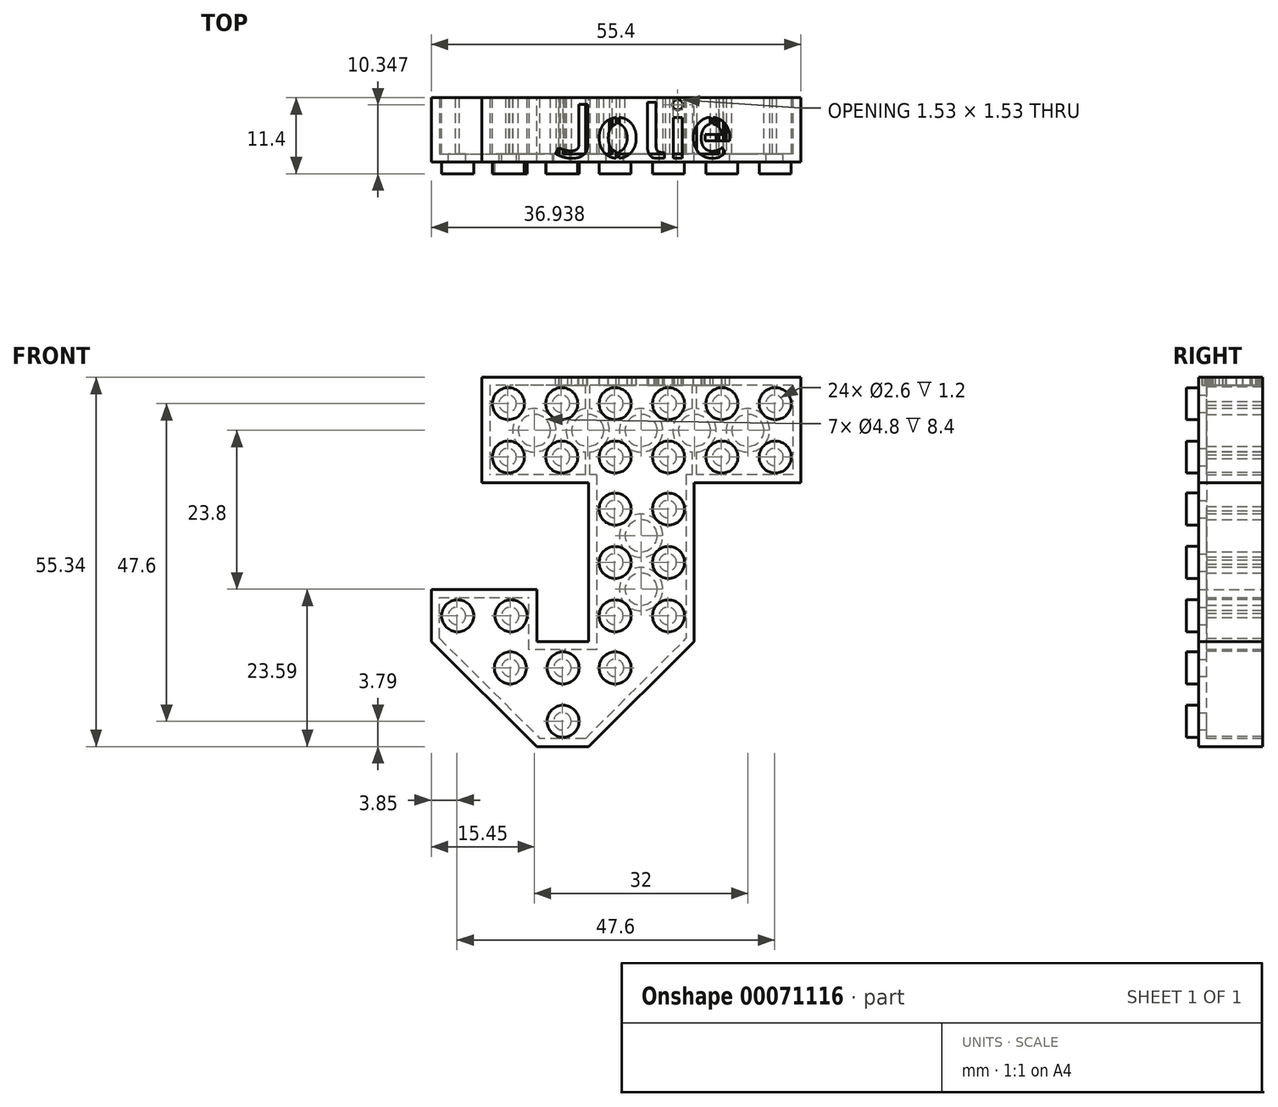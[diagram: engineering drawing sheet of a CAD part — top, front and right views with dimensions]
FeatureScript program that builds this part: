
annotation { "Feature Type Name" : "Feature", "Feature Type Description" : "" }
export const myFeature = defineFeature(function(context is Context, id is Id, definition is map)
    precondition{}
    {
        {
            var Q0;
            Q0=qCreatedBy(makeId("Front.planeOp"),FACE);
            var sketch = newSketch(context, id + "F0", { "sketchPlane" : qUnion([Q0])});
            skLineSegment(sketch, "E0.rect.bottom", {"start": v(23.9, 7.9) * mm, "end": v(-23.9, 7.9) * mm});
            skLineSegment(sketch, "E0.rect.top", {"start": v(23.9, -7.9) * mm, "end": v(7.9, -7.9) * mm});
            skLineSegment(sketch, "E0.rect.left", {"start": v(23.9, 7.9) * mm, "end": v(23.9, -7.9) * mm});
            skLineSegment(sketch, "E0.rect.right", {"start": v(-23.9, 7.9) * mm, "end": v(-23.9, -7.9) * mm});
            skPoint(sketch, "E0.rect.middle", {"position": v(0, 0) * mm});
            skLineSegment(sketch, "E1.left", {"start": v(-7.9, -7.9) * mm, "end": v(-7.9, -31.7) * mm});
            skLineSegment(sketch, "E1.right", {"start": v(7.9, -7.9) * mm, "end": v(7.9, -31.7) * mm});
            skLineSegment(sketch, "E2", {"start": v(-7.9, -47.44) * mm, "end": v(7.9, -31.7) * mm});
            skLineSegment(sketch, "E3.bottom", {"start": v(-7.9, -31.7) * mm, "end": v(-15.7, -31.7) * mm});
            skLineSegment(sketch, "E3.top", {"start": v(-7.9, -47.44) * mm, "end": v(-15.7, -47.44) * mm});
            skLineSegment(sketch, "E4", {"start": v(-31.5, -31.7) * mm, "end": v(-15.7, -47.44) * mm});
            skLineSegment(sketch, "E5.right", {"start": v(-15.7, -31.7) * mm, "end": v(-15.7, -23.9) * mm});
            skLineSegment(sketch, "E5.left", {"start": v(-31.5, -31.7) * mm, "end": v(-31.5, -23.9) * mm});
            skLineSegment(sketch, "E5.top", {"start": v(-31.5, -23.9) * mm, "end": v(-15.7, -23.9) * mm});
            skLineSegment(sketch, "E6.trimOffspring", {"start": v(-7.9, -7.9) * mm, "end": v(-23.9, -7.9) * mm});
            skLineSegment(sketch, "E7", {"start": v(7.9, -7.9) * mm, "end": v(-7.9, -7.9) * mm, "construction": true});
            skLineSegment(sketch, "E8", {"start": v(7.9, -31.7) * mm, "end": v(-7.9, -31.7) * mm, "construction": true});
            skLineSegment(sketch, "E9", {"start": v(-7.9, -31.7) * mm, "end": v(-7.9, -31.7) * mm});
            skLineSegment(sketch, "E10", {"start": v(-7.9, -47.44) * mm, "end": v(-7.9, -31.7) * mm, "construction": true});
            skLineSegment(sketch, "E11", {"start": v(-15.7, -31.7) * mm, "end": v(-15.7, -47.44) * mm, "construction": true});
            skLineSegment(sketch, "E12", {"start": v(-15.7, -31.7) * mm, "end": v(-31.5, -31.7) * mm, "construction": true});
            skSolve(sketch);
        }
        {
            var Q0;
            Q0 = qSketchRegion(id + "F0", true);
            extrude(context, id + "F1", {"entities" : qUnion([Q0]), "depth" : 9.6 * mm});
        }
        {
            var Q0;
            Q0=makeQuery(id+"F0.imprint","IMPRINT",FACE,{"disambiguationData":[TD([[makeQuery(id+"F0.imprint","IMPRINT",EDGE,{"derivedFrom":sQuery(id+"F0.wireOp",EDGE,"E0.rect.bottom")}),1.0]])]});
            var sketch = newSketch(context, id + "F2", { "sketchPlane" : qUnion([Q0])});
            skLineSegment(sketch, "E13.0", {"start": v(-30.3, -31.2) * mm, "end": v(-16.9, -44.55) * mm});
            skLineSegment(sketch, "E13.1", {"start": v(-8.4, -46.24) * mm, "end": v(5, -32.9) * mm});
            skLineSegment(sketch, "E13.2", {"start": v(-8.4, -46.24) * mm, "end": v(-15.2, -46.24) * mm});
            skLineSegment(sketch, "E13.3", {"start": v(-6.7, -44.55) * mm, "end": v(6.7, -31.2) * mm});
            skLineSegment(sketch, "E13.4", {"start": v(-6.7, -32.9) * mm, "end": v(-16.9, -32.9) * mm});
            skLineSegment(sketch, "E13.5", {"start": v(-30.3, -31.2) * mm, "end": v(-30.3, -25.1) * mm});
            skLineSegment(sketch, "E13.6", {"start": v(-6.7, -6.7) * mm, "end": v(-6.7, -32.9) * mm});
            skLineSegment(sketch, "E13.7", {"start": v(-16.9, -32.9) * mm, "end": v(-16.9, -25.1) * mm});
            skLineSegment(sketch, "E13.8", {"start": v(-22.7, 6.7) * mm, "end": v(-22.7, -6.7) * mm});
            skLineSegment(sketch, "E13.9", {"start": v(6.7, -6.7) * mm, "end": v(6.7, -31.2) * mm});
            skLineSegment(sketch, "E13.10", {"start": v(-30.3, -25.1) * mm, "end": v(-16.9, -25.1) * mm});
            skLineSegment(sketch, "E13.11", {"start": v(-6.7, -6.7) * mm, "end": v(-22.7, -6.7) * mm});
            skLineSegment(sketch, "E13.12", {"start": v(22.7, 6.7) * mm, "end": v(-22.7, 6.7) * mm});
            skLineSegment(sketch, "E13.13", {"start": v(-28.6, -32.9) * mm, "end": v(-15.2, -46.24) * mm});
            skLineSegment(sketch, "E13.14", {"start": v(22.7, -6.7) * mm, "end": v(6.7, -6.7) * mm});
            skLineSegment(sketch, "E13.15", {"start": v(22.7, 6.7) * mm, "end": v(22.7, -6.7) * mm});
            skLineSegment(sketch, "E14.2", {"start": v(-15.2, -46.24) * mm, "end": v(-8.4, -46.24) * mm});
            skLineSegment(sketch, "E14.5", {"start": v(-30.3, -25.1) * mm, "end": v(-30.3, -31.2) * mm});
            skLineSegment(sketch, "E14.6", {"start": v(-22.7, -6.7) * mm, "end": v(-6.7, -6.7) * mm});
            skLineSegment(sketch, "E14.10", {"start": v(-16.9, -25.1) * mm, "end": v(-30.3, -25.1) * mm});
            skLineSegment(sketch, "E14.12", {"start": v(22.7, -6.7) * mm, "end": v(22.7, 6.7) * mm});
            skLineSegment(sketch, "E14.14", {"start": v(6.7, -31.2) * mm, "end": v(6.7, -6.7) * mm});
            skLineSegment(sketch, "E14.15", {"start": v(6.7, -6.7) * mm, "end": v(22.7, -6.7) * mm});
            skSolve(sketch);
        }
        {
            var Q0;
            Q0 = qSketchRegion(id + "F2", true);
            extrude(context, id + "F3", {"entities" : qUnion([Q0]), "operationType" : NewBodyOperationType.REMOVE, "depth" : 8.4 * mm});
        }
        {
            var Q0;
            Q0=makeQuery(id+"F1.opExtrude","CAP_FACE",FACE,{"disambiguationData":[OSD([sQuery(id+"F0.wireOp",EDGE,"E0.rect.bottom"),sQuery(id+"F0.wireOp",EDGE,"E0.rect.top"),sQuery(id+"F0.wireOp",EDGE,"E0.rect.left"),sQuery(id+"F0.wireOp",EDGE,"E0.rect.right"),sQuery(id+"F0.wireOp",EDGE,"E1.top"),sQuery(id+"F0.wireOp",EDGE,"E1.left"),sQuery(id+"F0.wireOp",EDGE,"E1.right")])],"isStart":false});
            var sketch = newSketch(context, id + "F4", { "sketchPlane" : qUnion([Q0])});
            skCircle(sketch, "E15", {"center": v(-19.95, 3.95) * mm, "radius": 2.4 * mm});
            skCircle(sketch, "E16.0.1.0", {"center": v(-19.95, -4.05) * mm, "radius": 2.4 * mm});
            skCircle(sketch, "E16.1.0.0", {"center": v(-11.95, 3.95) * mm, "radius": 2.4 * mm});
            skCircle(sketch, "E16.1.1.0", {"center": v(-11.95, -4.05) * mm, "radius": 2.4 * mm});
            skCircle(sketch, "E16.2.0.0", {"center": v(-3.95, 3.95) * mm, "radius": 2.4 * mm});
            skCircle(sketch, "E16.2.1.0", {"center": v(-3.95, -4.05) * mm, "radius": 2.4 * mm});
            skCircle(sketch, "E16.3.0.0", {"center": v(4.05, 3.95) * mm, "radius": 2.4 * mm});
            skCircle(sketch, "E16.3.1.0", {"center": v(4.05, -4.05) * mm, "radius": 2.4 * mm});
            skCircle(sketch, "E16.4.0.0", {"center": v(12.05, 3.95) * mm, "radius": 2.4 * mm});
            skCircle(sketch, "E16.4.1.0", {"center": v(12.05, -4.05) * mm, "radius": 2.4 * mm});
            skCircle(sketch, "E16.5.0.0", {"center": v(20.05, 3.95) * mm, "radius": 2.4 * mm});
            skCircle(sketch, "E16.5.1.0", {"center": v(20.05, -4.05) * mm, "radius": 2.4 * mm});
            skLineSegment(sketch, "E16.direction1", {"start": v(-19.95, 3.95) * mm, "end": v(-11.95, 3.95) * mm, "construction": true});
            skLineSegment(sketch, "E16.direction2", {"start": v(-19.95, 3.95) * mm, "end": v(-19.95, -4.05) * mm, "construction": true});
            skSolve(sketch);
        }
        {
            var Q0;
            Q0=makeQuery(id+"F4.imprint","IMPRINT",FACE,{"disambiguationData":[TD([[makeQuery(id+"F4.imprint","IMPRINT",EDGE,{"derivedFrom":sQuery(id+"F4.wireOp",EDGE,"E15")}),1.0]])]});
            var Q1;
            Q1=makeQuery(id+"F4.imprint","IMPRINT",FACE,{"disambiguationData":[TD([[makeQuery(id+"F4.imprint","IMPRINT",EDGE,{"derivedFrom":sQuery(id+"F4.wireOp",EDGE,"E16.0.1.0")}),1.0]])]});
            var Q2;
            Q2=makeQuery(id+"F4.imprint","IMPRINT",FACE,{"disambiguationData":[TD([[makeQuery(id+"F4.imprint","IMPRINT",EDGE,{"derivedFrom":sQuery(id+"F4.wireOp",EDGE,"E16.1.0.0")}),1.0]])]});
            var Q3;
            Q3=makeQuery(id+"F4.imprint","IMPRINT",FACE,{"disambiguationData":[TD([[makeQuery(id+"F4.imprint","IMPRINT",EDGE,{"derivedFrom":sQuery(id+"F4.wireOp",EDGE,"E16.1.1.0")}),1.0]])]});
            var Q4;
            Q4=makeQuery(id+"F4.imprint","IMPRINT",FACE,{"disambiguationData":[TD([[makeQuery(id+"F4.imprint","IMPRINT",EDGE,{"derivedFrom":sQuery(id+"F4.wireOp",EDGE,"E16.2.0.0")}),1.0]])]});
            var Q5;
            Q5=makeQuery(id+"F4.imprint","IMPRINT",FACE,{"disambiguationData":[TD([[makeQuery(id+"F4.imprint","IMPRINT",EDGE,{"derivedFrom":sQuery(id+"F4.wireOp",EDGE,"E16.2.1.0")}),1.0]])]});
            var Q6;
            Q6=makeQuery(id+"F4.imprint","IMPRINT",FACE,{"disambiguationData":[TD([[makeQuery(id+"F4.imprint","IMPRINT",EDGE,{"derivedFrom":sQuery(id+"F4.wireOp",EDGE,"E16.3.0.0")}),1.0]])]});
            var Q7;
            Q7=makeQuery(id+"F4.imprint","IMPRINT",FACE,{"disambiguationData":[TD([[makeQuery(id+"F4.imprint","IMPRINT",EDGE,{"derivedFrom":sQuery(id+"F4.wireOp",EDGE,"E16.3.1.0")}),1.0]])]});
            var Q8;
            Q8=makeQuery(id+"F4.imprint","IMPRINT",FACE,{"disambiguationData":[TD([[makeQuery(id+"F4.imprint","IMPRINT",EDGE,{"derivedFrom":sQuery(id+"F4.wireOp",EDGE,"E16.4.0.0")}),1.0]])]});
            var Q9;
            Q9=makeQuery(id+"F4.imprint","IMPRINT",FACE,{"disambiguationData":[TD([[makeQuery(id+"F4.imprint","IMPRINT",EDGE,{"derivedFrom":sQuery(id+"F4.wireOp",EDGE,"E16.4.1.0")}),1.0]])]});
            var Q10;
            Q10=makeQuery(id+"F4.imprint","IMPRINT",FACE,{"disambiguationData":[TD([[makeQuery(id+"F4.imprint","IMPRINT",EDGE,{"derivedFrom":sQuery(id+"F4.wireOp",EDGE,"E16.5.0.0")}),1.0]])]});
            var Q11;
            Q11=makeQuery(id+"F4.imprint","IMPRINT",FACE,{"disambiguationData":[TD([[makeQuery(id+"F4.imprint","IMPRINT",EDGE,{"derivedFrom":sQuery(id+"F4.wireOp",EDGE,"E16.5.1.0")}),1.0]])]});
            extrude(context, id + "F5", {"entities" : qUnion([Q0, Q1, Q2, Q3, Q4, Q5, Q6, Q7, Q8, Q9, Q10, Q11]), "operationType" : NewBodyOperationType.ADD, "depth" : 1.8 * mm});
        }
        {
            var Q0;
            Q0=makeQuery(id+"F4.imprint","IMPRINT",FACE,{"disambiguationData":[TD([[makeQuery(id+"F4.imprint","IMPRINT",EDGE,{"derivedFrom":sQuery(id+"F4.wireOp",EDGE,"E15")}),-1.0]])]});
            var sketch = newSketch(context, id + "F6", { "sketchPlane" : qUnion([Q0])});
            skCircle(sketch, "E17", {"center": v(-3.95, -11.85) * mm, "radius": 2.4 * mm});
            skCircle(sketch, "E18.0.1.0", {"center": v(-3.95, -19.85) * mm, "radius": 2.4 * mm});
            skCircle(sketch, "E18.0.2.0", {"center": v(-3.95, -27.85) * mm, "radius": 2.4 * mm});
            skCircle(sketch, "E18.1.0.0", {"center": v(4.05, -11.85) * mm, "radius": 2.4 * mm});
            skCircle(sketch, "E18.1.1.0", {"center": v(4.05, -19.85) * mm, "radius": 2.4 * mm});
            skCircle(sketch, "E18.1.2.0", {"center": v(4.05, -27.85) * mm, "radius": 2.4 * mm});
            skLineSegment(sketch, "E18.direction1", {"start": v(-3.95, -11.85) * mm, "end": v(4.05, -11.85) * mm, "construction": true});
            skLineSegment(sketch, "E18.direction2", {"start": v(-3.95, -11.85) * mm, "end": v(-3.95, -19.85) * mm, "construction": true});
            skSolve(sketch);
        }
        {
            var Q0;
            Q0 = qSketchRegion(id + "F6", true);
            extrude(context, id + "F7", {"entities" : qUnion([Q0]), "operationType" : NewBodyOperationType.ADD, "depth" : 1.8 * mm});
        }
        {
            var Q0;
            Q0=makeQuery(id+"F4.imprint","IMPRINT",FACE,{"disambiguationData":[TD([[makeQuery(id+"F4.imprint","IMPRINT",EDGE,{"derivedFrom":sQuery(id+"F4.wireOp",EDGE,"E15")}),-1.0]])]});
            var sketch = newSketch(context, id + "F8", { "sketchPlane" : qUnion([Q0])});
            skCircle(sketch, "E19", {"center": v(-11.75, -35.65) * mm, "radius": 2.4 * mm});
            skCircle(sketch, "E20.0.1.0", {"center": v(-11.75, -43.65) * mm, "radius": 2.4 * mm});
            skCircle(sketch, "E21", {"center": v(-27.55, -27.85) * mm, "radius": 2.4 * mm});
            skCircle(sketch, "E22.1.0.0", {"center": v(-19.55, -27.85) * mm, "radius": 2.4 * mm});
            skLineSegment(sketch, "E23", {"start": v(-11.75, -43.65) * mm, "end": v(-11.75, -35.65) * mm, "construction": true});
            skSolve(sketch);
        }
        {
            var Q0;
            Q0 = qSketchRegion(id + "F8", true);
            extrude(context, id + "F9", {"entities" : qUnion([Q0]), "operationType" : NewBodyOperationType.ADD, "depth" : 1.8 * mm});
        }
        {
            var Q0;
            Q0=makeQuery(id+"F8.imprint","IMPRINT",FACE,{"disambiguationData":[TD([[makeQuery(id+"F8.imprint","IMPRINT",EDGE,{"derivedFrom":sQuery(id+"F8.wireOp",EDGE,"E19")}),-1.0]])]});
            var sketch = newSketch(context, id + "F10", { "sketchPlane" : qUnion([Q0])});
            skCircle(sketch, "E24", {"center": v(-3.95, -35.65) * mm, "radius": 2.4 * mm});
            skCircle(sketch, "E25", {"center": v(-19.65, -35.65) * mm, "radius": 2.4 * mm});
            skSolve(sketch);
        }
        {
            var Q0;
            Q0 = qSketchRegion(id + "F10", true);
            extrude(context, id + "F11", {"entities" : qUnion([Q0]), "operationType" : NewBodyOperationType.ADD, "depth" : 1.8 * mm});
        }
        {
            var Q0;
            Q0=makeQuery(id+"F0.imprint","IMPRINT",FACE,{"disambiguationData":[TD([[makeQuery(id+"F0.imprint","IMPRINT",EDGE,{"derivedFrom":sQuery(id+"F0.wireOp",EDGE,"E0.rect.bottom")}),1.0]])]});
            cPlane(context, id + "F12", {"entities" : qUnion([Q0]), "cplaneType" : CPlaneType.OFFSET, "offset" : 8.4 * mm, "width" : 150 * mm, "height" : 150 * mm});
        }
        {
            var Q0;
            Q0=qCreatedBy(id+"F12.planeOp",FACE);
            var sketch = newSketch(context, id + "F13", { "sketchPlane" : qUnion([Q0])});
            skCircle(sketch, "E26", {"center": v(19.95, 3.95) * mm, "radius": 1.3 * mm});
            skCircle(sketch, "E27.0.1.0", {"center": v(19.95, -4.05) * mm, "radius": 1.3 * mm});
            skCircle(sketch, "E27.1.0.0", {"center": v(11.95, 3.95) * mm, "radius": 1.3 * mm});
            skCircle(sketch, "E27.1.1.0", {"center": v(11.95, -4.05) * mm, "radius": 1.3 * mm});
            skCircle(sketch, "E27.2.0.0", {"center": v(3.95, 3.95) * mm, "radius": 1.3 * mm});
            skCircle(sketch, "E27.2.1.0", {"center": v(3.95, -4.05) * mm, "radius": 1.3 * mm});
            skCircle(sketch, "E27.3.0.0", {"center": v(-4.05, 3.95) * mm, "radius": 1.3 * mm});
            skCircle(sketch, "E27.3.1.0", {"center": v(-4.05, -4.05) * mm, "radius": 1.3 * mm});
            skCircle(sketch, "E27.4.0.0", {"center": v(-12.05, 3.95) * mm, "radius": 1.3 * mm});
            skCircle(sketch, "E27.4.1.0", {"center": v(-12.05, -4.05) * mm, "radius": 1.3 * mm});
            skCircle(sketch, "E27.5.0.0", {"center": v(-20.05, 3.95) * mm, "radius": 1.3 * mm});
            skCircle(sketch, "E27.5.1.0", {"center": v(-20.05, -4.05) * mm, "radius": 1.3 * mm});
            skLineSegment(sketch, "E27.direction1", {"start": v(19.95, 3.95) * mm, "end": v(11.95, 3.95) * mm, "construction": true});
            skLineSegment(sketch, "E27.direction2", {"start": v(19.95, 3.95) * mm, "end": v(19.95, -4.05) * mm, "construction": true});
            skCircle(sketch, "E28", {"center": v(3.95, -11.85) * mm, "radius": 1.3 * mm});
            skCircle(sketch, "E29.0.1.0", {"center": v(3.95, -19.85) * mm, "radius": 1.3 * mm});
            skCircle(sketch, "E29.0.2.0", {"center": v(3.95, -27.85) * mm, "radius": 1.3 * mm});
            skCircle(sketch, "E29.1.0.0", {"center": v(-4.05, -11.85) * mm, "radius": 1.3 * mm});
            skCircle(sketch, "E29.1.1.0", {"center": v(-4.05, -19.85) * mm, "radius": 1.3 * mm});
            skCircle(sketch, "E29.1.2.0", {"center": v(-4.05, -27.85) * mm, "radius": 1.3 * mm});
            skLineSegment(sketch, "E29.direction1", {"start": v(3.95, -11.85) * mm, "end": v(-4.05, -11.85) * mm, "construction": true});
            skLineSegment(sketch, "E29.direction2", {"start": v(3.95, -11.85) * mm, "end": v(3.95, -19.85) * mm, "construction": true});
            skCircle(sketch, "E30", {"center": v(-3.95, -35.65) * mm, "radius": 1.3 * mm});
            skCircle(sketch, "E31", {"center": v(-11.85, -35.65) * mm, "radius": 1.3 * mm});
            skCircle(sketch, "E32", {"center": v(-19.65, -35.65) * mm, "radius": 1.3 * mm});
            skCircle(sketch, "E33", {"center": v(-19.65, -27.85) * mm, "radius": 1.3 * mm});
            skCircle(sketch, "E34", {"center": v(-11.85, -43.65) * mm, "radius": 1.3 * mm});
            skCircle(sketch, "E35", {"center": v(-27.65, -27.85) * mm, "radius": 1.3 * mm});
            skSolve(sketch);
        }
        {
            var Q0;
            Q0 = qSketchRegion(id + "F13", true);
            extrude(context, id + "F14", {"entities" : qUnion([Q0]), "operationType" : NewBodyOperationType.REMOVE, "depth" : 1.2 * mm});
        }
        {
            var Q0;
            Q0=qCreatedBy(id+"F12.planeOp",FACE);
            var sketch = newSketch(context, id + "F15", { "sketchPlane" : qUnion([Q0])});
            skLineSegment(sketch, "E36", {"start": v(22.74, 6.74) * mm, "end": v(9.34, -6.66) * mm, "construction": true});
            skLineSegment(sketch, "E37", {"start": v(22.7, -6.8) * mm, "end": v(9.62, 6.28) * mm, "construction": true});
            skCircle(sketch, "E38", {"center": v(15.95, -0.05) * mm, "radius": 3.25 * mm});
            skCircle(sketch, "E39.1.0.0", {"center": v(7.95, -0.05) * mm, "radius": 3.25 * mm});
            skCircle(sketch, "E39.2.0.0", {"center": v(-0.05, -0.05) * mm, "radius": 3.25 * mm});
            skCircle(sketch, "E39.3.0.0", {"center": v(-8.05, -0.05) * mm, "radius": 3.25 * mm});
            skCircle(sketch, "E39.4.0.0", {"center": v(-16.05, -0.05) * mm, "radius": 3.25 * mm});
            skLineSegment(sketch, "E39.direction1", {"start": v(15.95, -0.05) * mm, "end": v(7.95, -0.05) * mm, "construction": true});
            skLineSegment(sketch, "E40", {"start": v(6.74, -9.06) * mm, "end": v(-5.78, -21.58) * mm, "construction": true});
            skLineSegment(sketch, "E41", {"start": v(6.08, -21.98) * mm, "end": v(-6.32, -9.58) * mm, "construction": true});
            skCircle(sketch, "E42", {"center": v(-0.05, -15.85) * mm, "radius": 3.25 * mm});
            skCircle(sketch, "E43.0.1.0", {"center": v(-0.05, -23.85) * mm, "radius": 3.25 * mm});
            skLineSegment(sketch, "E43.direction1", {"start": v(-0.05, -15.85) * mm, "end": v(7.95, -15.85) * mm, "construction": true});
            skLineSegment(sketch, "E43.direction2", {"start": v(-0.05, -15.85) * mm, "end": v(-0.05, -23.85) * mm, "construction": true});
            skSolve(sketch);
        }
        {
            var Q0;
            Q0 = qSketchRegion(id + "F15", true);
            extrude(context, id + "F16", {"entities" : qUnion([Q0]), "operationType" : NewBodyOperationType.ADD, "oppositeDirection" : true, "depth" : 8.4 * mm});
        }
        {
            var Q0;
            Q0=makeQuery(id+"F0.imprint","IMPRINT",FACE,{"disambiguationData":[TD([[makeQuery(id+"F0.imprint","IMPRINT",EDGE,{"derivedFrom":sQuery(id+"F0.wireOp",EDGE,"E0.rect.bottom")}),1.0]])]});
            var sketch = newSketch(context, id + "F17", { "sketchPlane" : qUnion([Q0])});
            skCircle(sketch, "E44", {"center": v(15.95, -0.05) * mm, "radius": 2.4 * mm});
            skCircle(sketch, "E45", {"center": v(-0.05, -15.85) * mm, "radius": 2.4 * mm});
            skCircle(sketch, "E46.1.0.0", {"center": v(7.95, -0.05) * mm, "radius": 2.4 * mm});
            skCircle(sketch, "E46.2.0.0", {"center": v(-0.05, -0.05) * mm, "radius": 2.4 * mm});
            skCircle(sketch, "E46.3.0.0", {"center": v(-8.05, -0.05) * mm, "radius": 2.4 * mm});
            skCircle(sketch, "E46.4.0.0", {"center": v(-16.05, -0.05) * mm, "radius": 2.4 * mm});
            skLineSegment(sketch, "E46.direction1", {"start": v(15.95, -0.05) * mm, "end": v(7.95, -0.05) * mm, "construction": true});
            skCircle(sketch, "E47.0.1.0", {"center": v(-0.05, -23.85) * mm, "radius": 2.4 * mm});
            skLineSegment(sketch, "E47.direction1", {"start": v(-0.05, -15.85) * mm, "end": v(7.95, -15.85) * mm, "construction": true});
            skLineSegment(sketch, "E47.direction2", {"start": v(-0.05, -15.85) * mm, "end": v(-0.05, -23.85) * mm, "construction": true});
            skSolve(sketch);
        }
        {
            var Q0;
            Q0=makeQuery(id+"F17.imprint","IMPRINT",FACE,{"disambiguationData":[TD([[makeQuery(id+"F17.imprint","IMPRINT",EDGE,{"derivedFrom":sQuery(id+"F17.wireOp",EDGE,"E44")}),1.0]])]});
            var Q1;
            Q1=makeQuery(id+"F17.imprint","IMPRINT",FACE,{"disambiguationData":[TD([[makeQuery(id+"F17.imprint","IMPRINT",EDGE,{"derivedFrom":sQuery(id+"F17.wireOp",EDGE,"E46.1.0.0")}),1.0]])]});
            var Q2;
            Q2=makeQuery(id+"F17.imprint","IMPRINT",FACE,{"disambiguationData":[TD([[makeQuery(id+"F17.imprint","IMPRINT",EDGE,{"derivedFrom":sQuery(id+"F17.wireOp",EDGE,"E45")}),1.0]])]});
            var Q3;
            Q3=makeQuery(id+"F17.imprint","IMPRINT",FACE,{"disambiguationData":[TD([[makeQuery(id+"F17.imprint","IMPRINT",EDGE,{"derivedFrom":sQuery(id+"F17.wireOp",EDGE,"E47.0.1.0")}),1.0]])]});
            var Q4;
            Q4=makeQuery(id+"F17.imprint","IMPRINT",FACE,{"disambiguationData":[TD([[makeQuery(id+"F17.imprint","IMPRINT",EDGE,{"derivedFrom":sQuery(id+"F17.wireOp",EDGE,"E46.4.0.0")}),1.0]])]});
            var Q5;
            Q5=makeQuery(id+"F17.imprint","IMPRINT",FACE,{"disambiguationData":[TD([[makeQuery(id+"F17.imprint","IMPRINT",EDGE,{"derivedFrom":sQuery(id+"F17.wireOp",EDGE,"E46.3.0.0")}),1.0]])]});
            var Q6;
            Q6=makeQuery(id+"F17.imprint","IMPRINT",FACE,{"disambiguationData":[TD([[makeQuery(id+"F17.imprint","IMPRINT",EDGE,{"derivedFrom":sQuery(id+"F17.wireOp",EDGE,"E46.2.0.0")}),1.0]])]});
            extrude(context, id + "F18", {"entities" : qUnion([Q0, Q1, Q2, Q3, Q4, Q5, Q6]), "operationType" : NewBodyOperationType.REMOVE, "depth" : 8.4 * mm});
        }
        {
            var Q0;
            Q0=qCreatedBy(id+"F12.planeOp",FACE);
            var sketch = newSketch(context, id + "F19", { "sketchPlane" : qUnion([Q0])});
            skLineSegment(sketch, "E48.bottom", {"start": v(8.25, -6.7) * mm, "end": v(7.65, -6.7) * mm});
            skLineSegment(sketch, "E48.top", {"start": v(8.25, -2.7) * mm, "end": v(7.65, -2.7) * mm});
            skLineSegment(sketch, "E48.left", {"start": v(8.25, -6.7) * mm, "end": v(8.25, -2.7) * mm});
            skLineSegment(sketch, "E48.right", {"start": v(7.65, -6.7) * mm, "end": v(7.65, -2.7) * mm});
            skLineSegment(sketch, "E49.0.1.0", {"start": v(8.25, 2.7) * mm, "end": v(8.25, 6.7) * mm});
            skLineSegment(sketch, "E49.0.1.1", {"start": v(8.25, 6.7) * mm, "end": v(7.65, 6.7) * mm});
            skLineSegment(sketch, "E49.0.1.2", {"start": v(7.65, 2.7) * mm, "end": v(7.65, 6.7) * mm});
            skLineSegment(sketch, "E49.0.1.3", {"start": v(8.25, 2.7) * mm, "end": v(7.65, 2.7) * mm});
            skLineSegment(sketch, "E49.1.0.0", {"start": v(-7.75, -6.7) * mm, "end": v(-7.75, -2.7) * mm});
            skLineSegment(sketch, "E49.1.0.1", {"start": v(-7.75, -2.7) * mm, "end": v(-8.35, -2.7) * mm});
            skLineSegment(sketch, "E49.1.0.2", {"start": v(-8.35, -6.7) * mm, "end": v(-8.35, -2.7) * mm});
            skLineSegment(sketch, "E49.1.0.3", {"start": v(-7.75, -6.7) * mm, "end": v(-8.35, -6.7) * mm});
            skLineSegment(sketch, "E49.1.1.0", {"start": v(-7.75, 2.7) * mm, "end": v(-7.75, 6.7) * mm});
            skLineSegment(sketch, "E49.1.1.1", {"start": v(-7.75, 6.7) * mm, "end": v(-8.35, 6.7) * mm});
            skLineSegment(sketch, "E49.1.1.2", {"start": v(-8.35, 2.7) * mm, "end": v(-8.35, 6.7) * mm});
            skLineSegment(sketch, "E49.1.1.3", {"start": v(-7.75, 2.7) * mm, "end": v(-8.35, 2.7) * mm});
            skLineSegment(sketch, "E49.direction1", {"start": v(8.25, -6.7) * mm, "end": v(-7.75, -6.7) * mm, "construction": true});
            skLineSegment(sketch, "E49.direction2", {"start": v(8.25, -6.7) * mm, "end": v(8.25, 2.7) * mm, "construction": true});
            skSolve(sketch);
        }
        {
            var Q0;
            Q0 = qSketchRegion(id + "F19", true);
            var Q1;
            Q1=makeQuery(id+"F16.boolean.opBoolean","MERGE",FACE,{"derivedFrom":[makeQuery(id+"F1.opExtrude","CAP_FACE",FACE,{"disambiguationData":[OSD([sQuery(id+"F0.wireOp",EDGE,"E0.rect.bottom"),sQuery(id+"F0.wireOp",EDGE,"E0.rect.top"),sQuery(id+"F0.wireOp",EDGE,"E0.rect.left"),sQuery(id+"F0.wireOp",EDGE,"E0.rect.right"),sQuery(id+"F0.wireOp",EDGE,"E1.top"),sQuery(id+"F0.wireOp",EDGE,"E1.left"),sQuery(id+"F0.wireOp",EDGE,"E1.right")])],"isStart":true}),makeQuery(id+"F1.opExtrude","CAP_FACE",FACE,{"disambiguationData":[OSD([sQuery(id+"FJ1ACUDYxAhP0Kk_0.wireOp",EDGE,"Wucu8hu5-kGE4-iVw8-EwE2-y0JzsKfOnsuY"),sQuery(id+"FJ1ACUDYxAhP0Kk_0.wireOp",EDGE,"a33cc1b2-1836-41d1-88ad-fe0056d83a28.bottom"),sQuery(id+"FJ1ACUDYxAhP0Kk_0.wireOp",EDGE,"a33cc1b2-1836-41d1-88ad-fe0056d83a28.top"),sQuery(id+"FJ1ACUDYxAhP0Kk_0.wireOp",EDGE,"7wYbTLAZ-uymM-28nJ-zka1-vrEMmaOiro4r"),sQuery(id+"FJ1ACUDYxAhP0Kk_0.wireOp",EDGE,"40946cf3-8972-4417-9fa9-1b25ef5c2fd7.top"),sQuery(id+"FJ1ACUDYxAhP0Kk_0.wireOp",EDGE,"40946cf3-8972-4417-9fa9-1b25ef5c2fd7.left"),sQuery(id+"FJ1ACUDYxAhP0Kk_0.wireOp",EDGE,"40946cf3-8972-4417-9fa9-1b25ef5c2fd7.right"),sQuery(id+"FJ1ACUDYxAhP0Kk_0.wireOp",EDGE,"NUz24gwK-Pouy-i7gN-xPQZ-Jzt4TPqwj3US")])],"isStart":true})]});
            extrude(context, id + "F20", {"entities" : qUnion([Q0]), "operationType" : NewBodyOperationType.ADD, "endBound" : BoundingType.UP_TO_SURFACE, "oppositeDirection" : true, "endBoundEntityFace" : qUnion([Q1]), "depth" : 25 * mm});
        }
        {
            var Q0;
            Q0=qCreatedBy(id+"F12.planeOp",FACE);
            var sketch = newSketch(context, id + "F21", { "sketchPlane" : qUnion([Q0])});
            skLineSegment(sketch, "E50", {"start": v(19.95, 4) * mm, "end": v(19.95, -10.78) * mm, "construction": true});
            skLineSegment(sketch, "E51.bottom", {"start": v(20.25, -6.4) * mm, "end": v(19.65, -6.4) * mm});
            skLineSegment(sketch, "E51.top", {"start": v(20.25, -6.7) * mm, "end": v(19.65, -6.7) * mm});
            skLineSegment(sketch, "E51.left", {"start": v(19.65, -6.4) * mm, "end": v(19.65, -6.7) * mm});
            skLineSegment(sketch, "E51.right", {"start": v(20.25, -6.4) * mm, "end": v(20.25, -6.7) * mm});
            skLineSegment(sketch, "E52.0.1.0", {"start": v(20.25, 6.72) * mm, "end": v(19.65, 6.72) * mm});
            skLineSegment(sketch, "E52.0.1.1", {"start": v(19.65, 6.72) * mm, "end": v(19.65, 6.42) * mm});
            skLineSegment(sketch, "E52.0.1.2", {"start": v(20.25, 6.42) * mm, "end": v(19.65, 6.42) * mm});
            skLineSegment(sketch, "E52.0.1.3", {"start": v(20.25, 6.72) * mm, "end": v(20.25, 6.42) * mm});
            skLineSegment(sketch, "E52.1.0.0", {"start": v(12.25, -6.4) * mm, "end": v(11.65, -6.4) * mm});
            skLineSegment(sketch, "E52.1.0.1", {"start": v(11.65, -6.4) * mm, "end": v(11.65, -6.7) * mm});
            skLineSegment(sketch, "E52.1.0.2", {"start": v(12.25, -6.7) * mm, "end": v(11.65, -6.7) * mm});
            skLineSegment(sketch, "E52.1.0.3", {"start": v(12.25, -6.4) * mm, "end": v(12.25, -6.7) * mm});
            skLineSegment(sketch, "E52.1.1.0", {"start": v(12.25, 6.72) * mm, "end": v(11.65, 6.72) * mm});
            skLineSegment(sketch, "E52.1.1.1", {"start": v(11.65, 6.72) * mm, "end": v(11.65, 6.42) * mm});
            skLineSegment(sketch, "E52.1.1.2", {"start": v(12.25, 6.42) * mm, "end": v(11.65, 6.42) * mm});
            skLineSegment(sketch, "E52.1.1.3", {"start": v(12.25, 6.72) * mm, "end": v(12.25, 6.42) * mm});
            skLineSegment(sketch, "E52.2.1.0", {"start": v(4.25, 6.72) * mm, "end": v(3.65, 6.72) * mm});
            skLineSegment(sketch, "E52.2.1.1", {"start": v(3.65, 6.72) * mm, "end": v(3.65, 6.42) * mm});
            skLineSegment(sketch, "E52.2.1.2", {"start": v(4.25, 6.42) * mm, "end": v(3.65, 6.42) * mm});
            skLineSegment(sketch, "E52.2.1.3", {"start": v(4.25, 6.72) * mm, "end": v(4.25, 6.42) * mm});
            skLineSegment(sketch, "E52.3.1.0", {"start": v(-3.75, 6.72) * mm, "end": v(-4.35, 6.72) * mm});
            skLineSegment(sketch, "E52.3.1.1", {"start": v(-4.35, 6.72) * mm, "end": v(-4.35, 6.42) * mm});
            skLineSegment(sketch, "E52.3.1.2", {"start": v(-3.75, 6.42) * mm, "end": v(-4.35, 6.42) * mm});
            skLineSegment(sketch, "E52.3.1.3", {"start": v(-3.75, 6.72) * mm, "end": v(-3.75, 6.42) * mm});
            skLineSegment(sketch, "E52.4.0.0", {"start": v(-11.75, -6.4) * mm, "end": v(-12.35, -6.4) * mm});
            skLineSegment(sketch, "E52.4.0.1", {"start": v(-12.35, -6.4) * mm, "end": v(-12.35, -6.7) * mm});
            skLineSegment(sketch, "E52.4.0.2", {"start": v(-11.75, -6.7) * mm, "end": v(-12.35, -6.7) * mm});
            skLineSegment(sketch, "E52.4.0.3", {"start": v(-11.75, -6.4) * mm, "end": v(-11.75, -6.7) * mm});
            skLineSegment(sketch, "E52.4.1.0", {"start": v(-11.75, 6.72) * mm, "end": v(-12.35, 6.72) * mm});
            skLineSegment(sketch, "E52.4.1.1", {"start": v(-12.35, 6.72) * mm, "end": v(-12.35, 6.42) * mm});
            skLineSegment(sketch, "E52.4.1.2", {"start": v(-11.75, 6.42) * mm, "end": v(-12.35, 6.42) * mm});
            skLineSegment(sketch, "E52.4.1.3", {"start": v(-11.75, 6.72) * mm, "end": v(-11.75, 6.42) * mm});
            skLineSegment(sketch, "E52.5.0.0", {"start": v(-19.75, -6.4) * mm, "end": v(-20.35, -6.4) * mm});
            skLineSegment(sketch, "E52.5.0.1", {"start": v(-20.35, -6.4) * mm, "end": v(-20.35, -6.7) * mm});
            skLineSegment(sketch, "E52.5.0.2", {"start": v(-19.75, -6.7) * mm, "end": v(-20.35, -6.7) * mm});
            skLineSegment(sketch, "E52.5.0.3", {"start": v(-19.75, -6.4) * mm, "end": v(-19.75, -6.7) * mm});
            skLineSegment(sketch, "E52.5.1.0", {"start": v(-19.75, 6.72) * mm, "end": v(-20.35, 6.72) * mm});
            skLineSegment(sketch, "E52.5.1.1", {"start": v(-20.35, 6.72) * mm, "end": v(-20.35, 6.42) * mm});
            skLineSegment(sketch, "E52.5.1.2", {"start": v(-19.75, 6.42) * mm, "end": v(-20.35, 6.42) * mm});
            skLineSegment(sketch, "E52.5.1.3", {"start": v(-19.75, 6.72) * mm, "end": v(-19.75, 6.42) * mm});
            skLineSegment(sketch, "E52.direction1", {"start": v(19.65, -6.4) * mm, "end": v(11.65, -6.4) * mm, "construction": true});
            skLineSegment(sketch, "E52.direction2", {"start": v(19.65, -6.4) * mm, "end": v(19.65, 6.72) * mm, "construction": true});
            skLineSegment(sketch, "E53", {"start": v(9.92, -11.85) * mm, "end": v(-8.63, -11.85) * mm, "construction": true});
            skLineSegment(sketch, "E54.bottom", {"start": v(6.7, -11.55) * mm, "end": v(6.4, -11.55) * mm});
            skLineSegment(sketch, "E54.top", {"start": v(6.7, -12.15) * mm, "end": v(6.4, -12.15) * mm});
            skLineSegment(sketch, "E54.left", {"start": v(6.7, -11.55) * mm, "end": v(6.7, -12.15) * mm});
            skLineSegment(sketch, "E54.right", {"start": v(6.4, -11.55) * mm, "end": v(6.4, -12.15) * mm});
            skLineSegment(sketch, "E55.0.1.0", {"start": v(6.7, -19.55) * mm, "end": v(6.4, -19.55) * mm});
            skLineSegment(sketch, "E55.0.1.1", {"start": v(6.4, -19.55) * mm, "end": v(6.4, -20.15) * mm});
            skLineSegment(sketch, "E55.0.1.2", {"start": v(6.7, -20.15) * mm, "end": v(6.4, -20.15) * mm});
            skLineSegment(sketch, "E55.0.1.3", {"start": v(6.7, -19.55) * mm, "end": v(6.7, -20.15) * mm});
            skLineSegment(sketch, "E55.0.2.0", {"start": v(6.7, -27.55) * mm, "end": v(6.4, -27.55) * mm});
            skLineSegment(sketch, "E55.0.2.1", {"start": v(6.4, -27.55) * mm, "end": v(6.4, -28.15) * mm});
            skLineSegment(sketch, "E55.0.2.2", {"start": v(6.7, -28.15) * mm, "end": v(6.4, -28.15) * mm});
            skLineSegment(sketch, "E55.0.2.3", {"start": v(6.7, -27.55) * mm, "end": v(6.7, -28.15) * mm});
            skLineSegment(sketch, "E55.1.0.0", {"start": v(-6.42, -11.55) * mm, "end": v(-6.72, -11.55) * mm});
            skLineSegment(sketch, "E55.1.0.1", {"start": v(-6.72, -11.55) * mm, "end": v(-6.72, -12.15) * mm});
            skLineSegment(sketch, "E55.1.0.2", {"start": v(-6.42, -12.15) * mm, "end": v(-6.72, -12.15) * mm});
            skLineSegment(sketch, "E55.1.0.3", {"start": v(-6.42, -11.55) * mm, "end": v(-6.42, -12.15) * mm});
            skLineSegment(sketch, "E55.1.1.0", {"start": v(-6.42, -19.55) * mm, "end": v(-6.72, -19.55) * mm});
            skLineSegment(sketch, "E55.1.1.1", {"start": v(-6.72, -19.55) * mm, "end": v(-6.72, -20.15) * mm});
            skLineSegment(sketch, "E55.1.1.2", {"start": v(-6.42, -20.15) * mm, "end": v(-6.72, -20.15) * mm});
            skLineSegment(sketch, "E55.1.1.3", {"start": v(-6.42, -19.55) * mm, "end": v(-6.42, -20.15) * mm});
            skLineSegment(sketch, "E55.1.2.0", {"start": v(-6.42, -27.55) * mm, "end": v(-6.72, -27.55) * mm});
            skLineSegment(sketch, "E55.1.2.1", {"start": v(-6.72, -27.55) * mm, "end": v(-6.72, -28.15) * mm});
            skLineSegment(sketch, "E55.1.2.2", {"start": v(-6.42, -28.15) * mm, "end": v(-6.72, -28.15) * mm});
            skLineSegment(sketch, "E55.1.2.3", {"start": v(-6.42, -27.55) * mm, "end": v(-6.42, -28.15) * mm});
            skLineSegment(sketch, "E55.direction1", {"start": v(6.4, -11.55) * mm, "end": v(-6.72, -11.55) * mm, "construction": true});
            skLineSegment(sketch, "E55.direction2", {"start": v(6.4, -11.55) * mm, "end": v(6.4, -19.55) * mm, "construction": true});
            skLineSegment(sketch, "E56.0.1.0", {"start": v(-19.35, -25.4) * mm, "end": v(-19.95, -25.4) * mm});
            skLineSegment(sketch, "E56.0.1.1", {"start": v(-19.35, -25.1) * mm, "end": v(-19.35, -25.4) * mm});
            skLineSegment(sketch, "E56.0.1.2", {"start": v(-19.35, -25.1) * mm, "end": v(-19.95, -25.1) * mm});
            skLineSegment(sketch, "E56.0.1.3", {"start": v(-19.95, -25.1) * mm, "end": v(-19.95, -25.4) * mm});
            skLineSegment(sketch, "E56.1.1.0", {"start": v(-27.35, -25.4) * mm, "end": v(-27.95, -25.4) * mm});
            skLineSegment(sketch, "E56.1.1.1", {"start": v(-27.35, -25.1) * mm, "end": v(-27.35, -25.4) * mm});
            skLineSegment(sketch, "E56.1.1.2", {"start": v(-27.35, -25.1) * mm, "end": v(-27.95, -25.1) * mm});
            skLineSegment(sketch, "E56.1.1.3", {"start": v(-27.95, -25.1) * mm, "end": v(-27.95, -25.4) * mm});
            skLineSegment(sketch, "E56.direction1", {"start": v(-19.95, -30.5) * mm, "end": v(-27.95, -30.5) * mm, "construction": true});
            skLineSegment(sketch, "E56.direction2", {"start": v(-19.95, -30.5) * mm, "end": v(-19.95, -25.4) * mm, "construction": true});
            skLineSegment(sketch, "E57", {"start": v(23.6, -4.05) * mm, "end": v(16, -4.05) * mm, "construction": true});
            skLineSegment(sketch, "E58.bottom", {"start": v(22.7, -3.75) * mm, "end": v(22.4, -3.75) * mm});
            skLineSegment(sketch, "E58.top", {"start": v(22.7, -4.35) * mm, "end": v(22.4, -4.35) * mm});
            skLineSegment(sketch, "E58.left", {"start": v(22.7, -3.75) * mm, "end": v(22.7, -4.35) * mm});
            skLineSegment(sketch, "E58.right", {"start": v(22.4, -3.75) * mm, "end": v(22.4, -4.35) * mm});
            skLineSegment(sketch, "E59.0.1.0", {"start": v(22.7, 4.25) * mm, "end": v(22.4, 4.25) * mm});
            skLineSegment(sketch, "E59.0.1.1", {"start": v(22.4, 4.25) * mm, "end": v(22.4, 3.65) * mm});
            skLineSegment(sketch, "E59.0.1.2", {"start": v(22.7, 3.65) * mm, "end": v(22.4, 3.65) * mm});
            skLineSegment(sketch, "E59.0.1.3", {"start": v(22.7, 4.25) * mm, "end": v(22.7, 3.65) * mm});
            skLineSegment(sketch, "E59.1.0.0", {"start": v(-22.4, -3.75) * mm, "end": v(-22.7, -3.75) * mm});
            skLineSegment(sketch, "E59.1.0.1", {"start": v(-22.7, -3.75) * mm, "end": v(-22.7, -4.35) * mm});
            skLineSegment(sketch, "E59.1.0.2", {"start": v(-22.4, -4.35) * mm, "end": v(-22.7, -4.35) * mm});
            skLineSegment(sketch, "E59.1.0.3", {"start": v(-22.4, -3.75) * mm, "end": v(-22.4, -4.35) * mm});
            skLineSegment(sketch, "E59.1.1.0", {"start": v(-22.4, 4.25) * mm, "end": v(-22.7, 4.25) * mm});
            skLineSegment(sketch, "E59.1.1.1", {"start": v(-22.7, 4.25) * mm, "end": v(-22.7, 3.65) * mm});
            skLineSegment(sketch, "E59.1.1.2", {"start": v(-22.4, 3.65) * mm, "end": v(-22.7, 3.65) * mm});
            skLineSegment(sketch, "E59.1.1.3", {"start": v(-22.4, 4.25) * mm, "end": v(-22.4, 3.65) * mm});
            skLineSegment(sketch, "E59.direction1", {"start": v(22.4, -3.75) * mm, "end": v(-22.7, -3.75) * mm, "construction": true});
            skLineSegment(sketch, "E59.direction2", {"start": v(22.4, -3.75) * mm, "end": v(22.4, 4.25) * mm, "construction": true});
            skLineSegment(sketch, "E60", {"start": v(4.05, -7.9) * mm, "end": v(4.05, -21.73) * mm, "construction": true});
            skLineSegment(sketch, "E61.bottom", {"start": v(-11.55, -32.9) * mm, "end": v(-12.15, -32.9) * mm});
            skLineSegment(sketch, "E61.top", {"start": v(-11.55, -33.2) * mm, "end": v(-12.15, -33.2) * mm});
            skLineSegment(sketch, "E61.left", {"start": v(-11.55, -32.9) * mm, "end": v(-11.55, -33.2) * mm});
            skLineSegment(sketch, "E61.right", {"start": v(-12.15, -32.9) * mm, "end": v(-12.15, -33.2) * mm});
            skLineSegment(sketch, "E62.bottom", {"start": v(-11.55, -45.94) * mm, "end": v(-12.15, -45.94) * mm});
            skLineSegment(sketch, "E62.top", {"start": v(-11.55, -46.24) * mm, "end": v(-12.15, -46.24) * mm});
            skLineSegment(sketch, "E62.left", {"start": v(-11.55, -45.94) * mm, "end": v(-11.55, -46.24) * mm});
            skLineSegment(sketch, "E62.right", {"start": v(-12.15, -45.94) * mm, "end": v(-12.15, -46.24) * mm});
            skLineSegment(sketch, "E63.bottom", {"start": v(-16.9, -27.55) * mm, "end": v(-17.2, -27.55) * mm});
            skLineSegment(sketch, "E63.top", {"start": v(-16.9, -28.15) * mm, "end": v(-17.2, -28.15) * mm});
            skLineSegment(sketch, "E63.left", {"start": v(-16.9, -27.55) * mm, "end": v(-16.9, -28.15) * mm});
            skLineSegment(sketch, "E63.right", {"start": v(-17.2, -27.55) * mm, "end": v(-17.2, -28.15) * mm});
            skLineSegment(sketch, "E64.bottom", {"start": v(-30, -27.55) * mm, "end": v(-30.3, -27.55) * mm});
            skLineSegment(sketch, "E64.top", {"start": v(-30, -28.15) * mm, "end": v(-30.3, -28.15) * mm});
            skLineSegment(sketch, "E64.left", {"start": v(-30, -27.55) * mm, "end": v(-30, -28.15) * mm});
            skLineSegment(sketch, "E64.right", {"start": v(-30.3, -27.55) * mm, "end": v(-30.3, -28.15) * mm});
            skSolve(sketch);
        }
        {
            var Q0;
            Q0 = qSketchRegion(id + "F21", true);
            var Q1;
            Q1=makeQuery(id+"F20.boolean.opBoolean","MERGE",FACE,{"derivedFrom":[makeQuery(id+"F16.boolean.opBoolean","MERGE",FACE,{"derivedFrom":[makeQuery(id+"F1.opExtrude","CAP_FACE",FACE,{"disambiguationData":[OSD([sQuery(id+"F0.wireOp",EDGE,"E0.rect.bottom"),sQuery(id+"F0.wireOp",EDGE,"E0.rect.top"),sQuery(id+"F0.wireOp",EDGE,"E0.rect.left"),sQuery(id+"F0.wireOp",EDGE,"E0.rect.right"),sQuery(id+"F0.wireOp",EDGE,"E1.top"),sQuery(id+"F0.wireOp",EDGE,"E1.left"),sQuery(id+"F0.wireOp",EDGE,"E1.right")])],"isStart":true}),makeQuery(id+"F1.opExtrude","CAP_FACE",FACE,{"disambiguationData":[OSD([sQuery(id+"FJ1ACUDYxAhP0Kk_0.wireOp",EDGE,"Wucu8hu5-kGE4-iVw8-EwE2-y0JzsKfOnsuY"),sQuery(id+"FJ1ACUDYxAhP0Kk_0.wireOp",EDGE,"a33cc1b2-1836-41d1-88ad-fe0056d83a28.bottom"),sQuery(id+"FJ1ACUDYxAhP0Kk_0.wireOp",EDGE,"a33cc1b2-1836-41d1-88ad-fe0056d83a28.top"),sQuery(id+"FJ1ACUDYxAhP0Kk_0.wireOp",EDGE,"7wYbTLAZ-uymM-28nJ-zka1-vrEMmaOiro4r"),sQuery(id+"FJ1ACUDYxAhP0Kk_0.wireOp",EDGE,"40946cf3-8972-4417-9fa9-1b25ef5c2fd7.top"),sQuery(id+"FJ1ACUDYxAhP0Kk_0.wireOp",EDGE,"40946cf3-8972-4417-9fa9-1b25ef5c2fd7.left"),sQuery(id+"FJ1ACUDYxAhP0Kk_0.wireOp",EDGE,"40946cf3-8972-4417-9fa9-1b25ef5c2fd7.right"),sQuery(id+"FJ1ACUDYxAhP0Kk_0.wireOp",EDGE,"NUz24gwK-Pouy-i7gN-xPQZ-Jzt4TPqwj3US")])],"isStart":true})]}),makeQuery(id+"F16.opExtrude","CAP_FACE",FACE,{"disambiguationData":[OSD([sQuery(id+"F15.wireOp",EDGE,"E39.1.0.0")])],"isStart":false}),makeQuery(id+"F16.opExtrude","CAP_FACE",FACE,{"disambiguationData":[OSD([sQuery(id+"F15.wireOp",EDGE,"E39.3.0.0")])],"isStart":false}),makeQuery(id+"F20.opExtrude","CAP_FACE",FACE,{"disambiguationData":[OSD([sQuery(id+"F19.wireOp",EDGE,"E48.bottom"),sQuery(id+"F19.wireOp",EDGE,"E48.top"),sQuery(id+"F19.wireOp",EDGE,"E48.left"),sQuery(id+"F19.wireOp",EDGE,"E48.right")])],"isStart":false}),makeQuery(id+"F20.opExtrude","CAP_FACE",FACE,{"disambiguationData":[OSD([sQuery(id+"F19.wireOp",EDGE,"E49.0.1.0"),sQuery(id+"F19.wireOp",EDGE,"E49.0.1.1"),sQuery(id+"F19.wireOp",EDGE,"E49.0.1.2"),sQuery(id+"F19.wireOp",EDGE,"E49.0.1.3")])],"isStart":false}),makeQuery(id+"F20.opExtrude","CAP_FACE",FACE,{"disambiguationData":[OSD([sQuery(id+"F19.wireOp",EDGE,"E49.1.0.0"),sQuery(id+"F19.wireOp",EDGE,"E49.1.0.1"),sQuery(id+"F19.wireOp",EDGE,"E49.1.0.2"),sQuery(id+"F19.wireOp",EDGE,"E49.1.0.3")])],"isStart":false}),makeQuery(id+"F20.opExtrude","CAP_FACE",FACE,{"disambiguationData":[OSD([sQuery(id+"F19.wireOp",EDGE,"E49.1.1.0"),sQuery(id+"F19.wireOp",EDGE,"E49.1.1.1"),sQuery(id+"F19.wireOp",EDGE,"E49.1.1.2"),sQuery(id+"F19.wireOp",EDGE,"E49.1.1.3")])],"isStart":false})]});
            extrude(context, id + "F22", {"entities" : qUnion([Q0]), "operationType" : NewBodyOperationType.ADD, "endBound" : BoundingType.UP_TO_SURFACE, "oppositeDirection" : true, "endBoundEntityFace" : qUnion([Q1]), "depth" : 25 * mm});
        }
        {
            var Q0;
            Q0=makeQuery(id+"F1.opExtrude","SWEPT_FACE",FACE,{"disambiguationData":[OSD([sQuery(id+"F0.wireOp",EDGE,"E0.rect.bottom")])]});
            var sketch = newSketch(context, id + "F23", { "sketchPlane" : qUnion([Q0])});
            skText(sketch, "E65", { "text": "Jolie", "fontName": "AllertaStencil-Regular.ttf"});
            const initialGuessF23  = {"E65": [-0.01317, -0.00903, 1, 0, 0.0079]};
            skSetInitialGuess(sketch, initialGuessF23);
            skSolve(sketch);
        }
        {
            var Q0;
            Q0 = qSketchRegion(id + "F23", true);
            extrude(context, id + "F24", {"entities" : qUnion([Q0]), "operationType" : NewBodyOperationType.REMOVE, "oppositeDirection" : true, "depth" : 1.2 * mm});
        }
    });
